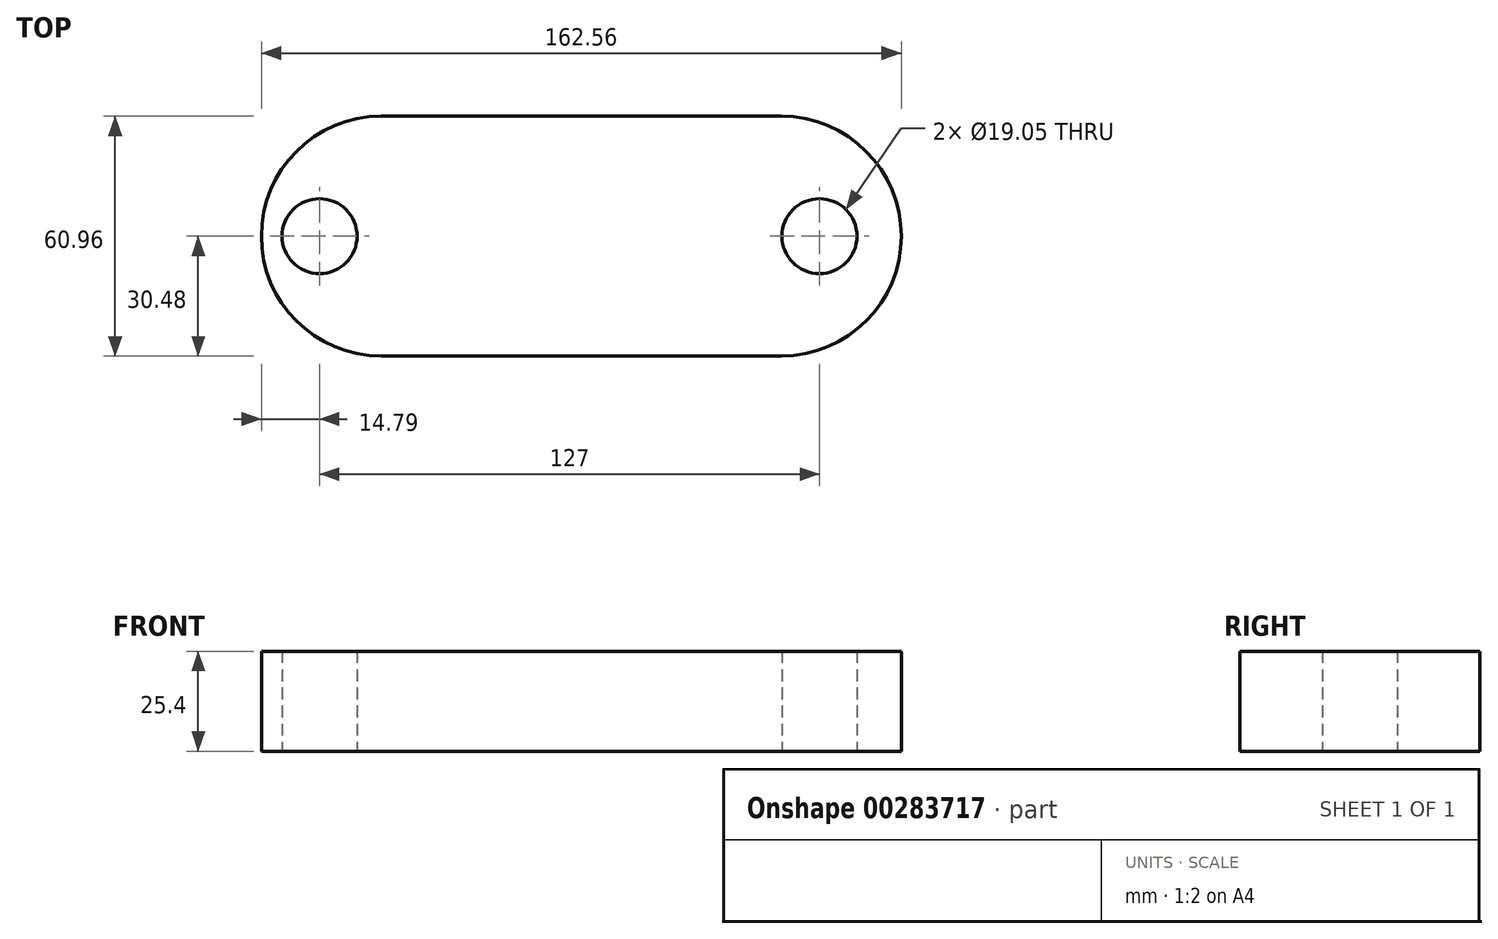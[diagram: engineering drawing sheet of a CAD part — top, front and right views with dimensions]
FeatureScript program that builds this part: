
annotation { "Feature Type Name" : "Feature", "Feature Type Description" : "" }
export const myFeature = defineFeature(function(context is Context, id is Id, definition is map)
    precondition{}
    {
        {
            var Q0;
            Q0=qCreatedBy(makeId("Top.planeOp"),FACE);
            var sketch = newSketch(context, id + "F0", { "sketchPlane" : qUnion([Q0])});
            skLineSegment(sketch, "E0", {"start": v(-47.8, 30.48) * mm, "end": v(53.8, 30.48) * mm});
            skLineSegment(sketch, "E1", {"start": v(-47.8, -30.48) * mm, "end": v(53.8, -30.48) * mm});
            skArc(sketch, "E2", {"start": v(53.8, -30.48) * mm, "mid": v(84.27, 0) * mm, "end": v(53.8, 30.48) * mm});
            skArc(sketch, "E3", {"start": v(-47.8, 30.48) * mm, "mid": v(-78.29, 0) * mm, "end": v(-47.8, -30.48) * mm});
            skSolve(sketch);
        }
        {
            var Q0;
            Q0=makeQuery(id+"F0.imprint","IMPRINT",FACE,{"disambiguationData":[TD([[makeQuery(id+"F0.imprint","IMPRINT",EDGE,{"derivedFrom":sQuery(id+"F0.wireOp",EDGE,"E0")}),-1.0]])]});
            var sketch = newSketch(context, id + "F1", { "sketchPlane" : qUnion([Q0])});
            skCircle(sketch, "E4", {"center": v(-63.5, 0) * mm, "radius": 9.53 * mm});
            skCircle(sketch, "E5", {"center": v(63.5, 0) * mm, "radius": 9.53 * mm});
            skSolve(sketch);
        }
        {
            var Q0;
            Q0=makeQuery(id+"F1.imprint","IMPRINT",FACE,{"disambiguationData":[TD([[makeQuery(id+"F1.imprint","IMPRINT",EDGE,{"derivedFrom":sQuery(id+"F1.wireOp",EDGE,"E4")}),-1.0]])]});
            extrude(context, id + "F2", {"entities" : qUnion([Q0]), "depth" : 25.4 * mm});
        }
    });
